# Revit family: 403109d2-fda5-4698-ab24-676e46adb4a7
name_source: partatom
category: Plumbing Fixtures
revit_build: Autodesk Revit 2016 (Build: 20161004_0715(x64)
units: mm (PartAtom-declared; Revit-internal decimal feet)

## family parameters
Cut with Voids When Loaded = No
Host = Face
OmniClass Number = 23.45.55.14
OmniClass Title = Single Faucets
Part Type = Normal
Room Calculation Point = No
Round Connector Dimension = Use Diameter
Shared = No

## types (1)
- SF380
    Assembly Code = D2010430
    CW Connection = No
    CWFU = 0
    Default Elevation = 48 "
    Depth = 3.23 "
    Description = Ligature Resistant Metering Faucet
    Finish = Metal - BSP - Chrome - Polished
    HW Connection = No
    HWFU = 0
    Height = 4.39 "
    Manufacturer = Behavioral Safety Products
    Model = SF380
    Product Documentation Link = http://besafeprod.com
    Product Page URL = http://besafeprod.com
    Product data url = https://bimobject.com
    Type Image = <None>
    URL = http://besafeprod.com
    Vent Connection = No
    Waste Connection = No
    Water In Connection Description 1 = Hot Water Connection
    Water In Connection Description 2 = Cold Water Connection
    Width = 7.82 "

## geometry (parser evidence)
native form markers: Blend x16, Sweep x4
no freeform markers — native parametric forms only
